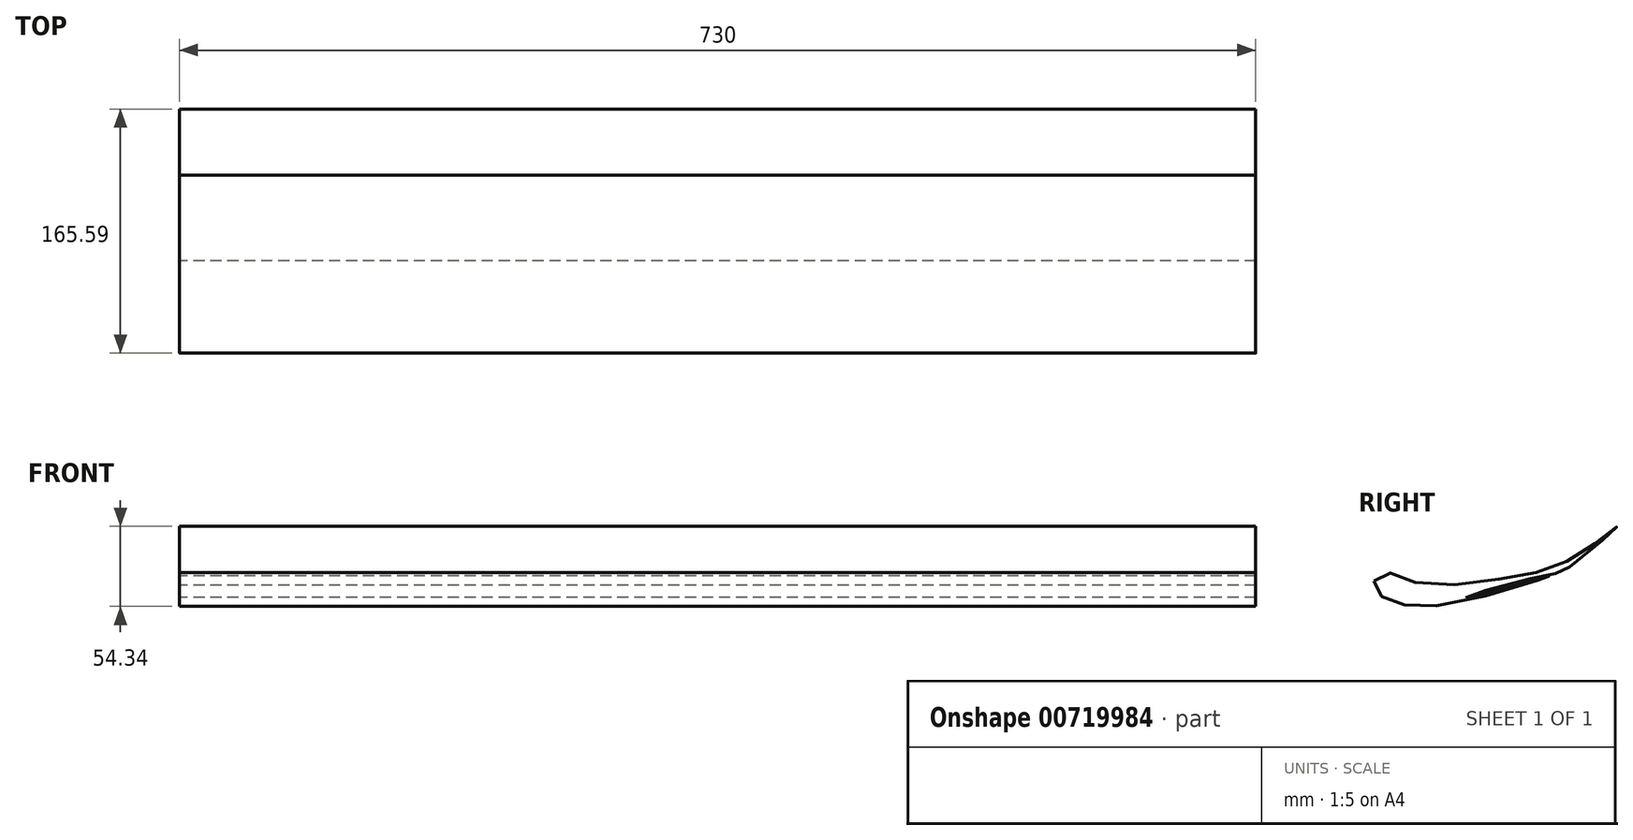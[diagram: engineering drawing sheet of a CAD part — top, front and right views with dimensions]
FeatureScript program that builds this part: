
annotation { "Feature Type Name" : "Feature", "Feature Type Description" : "" }
export const myFeature = defineFeature(function(context is Context, id is Id, definition is map)
    precondition{}
    {
        {
            var Q0;
            Q0=qCreatedBy(makeId("Right.planeOp"),FACE);
            var sketch = newSketch(context, id + "F0", { "sketchPlane" : qUnion([Q0])});
            skFitSpline(sketch, "E0", {"points": [v(-91.57, -32.12) * mm, v(-88.6, -40.7) * mm, v(-73.22, -47.81) * mm, v(-31.77, -46.04) * mm, v(28.63, -28.57) * mm, v(22.4, -30.35) * mm, v(2.28, -35.67) * mm, v(-29.1, -43.08) * mm, v(-25.85, -41.6) * mm, v(24.78, -28.27) * mm, v(33.07, -26.8) * mm, v(42.25, -21.76) * mm, v(73.63, 4.88) * mm, v(63.86, -2.52) * mm, v(34.25, -21.17) * mm, v(-3.64, -30.35) * mm, v(-61.08, -33.6) * mm, v(-82.4, -26.5) * mm, v(-91.57, -32.12) * mm]});
            skSolve(sketch);
        }
        {
            var Q0;
            Q0 = qSketchRegion(id + "F0", true);
            extrude(context, id + "F1", {"entities" : qUnion([Q0]), "endBound" : BoundingType.SYMMETRIC, "depth" : 730 * mm, "offsetDistance" : 25 * mm});
        }
        {
            var Q0;
            Q0=qCreatedBy(makeId("Right.planeOp"),FACE);
            var sketch = newSketch(context, id + "F2", { "sketchPlane" : qUnion([Q0])});
            skFitSpline(sketch, "E1", {"points": [v(48.46, -3.4) * mm, v(49.05, -6.96) * mm, v(55.86, -3.7) * mm, v(68.9, 7.55) * mm, v(82.8, 30.64) * mm, v(100.86, 72.38) * mm, v(89.61, 49) * mm, v(74.52, 20.28) * mm, v(58.82, 6.37) * mm, v(48.76, 0) * mm, v(48.46, -3.4) * mm]});
            skSolve(sketch);
        }
        {
            var Q0;
            Q0=sQuery(id+"F2.wireOp",EDGE,"E1");
            extrude(context, id + "F3", {"bodyType" : ToolBodyType.SURFACE, "surfaceEntities" : qUnion([Q0]), "endBound" : BoundingType.SYMMETRIC, "depth" : 730 * mm, "offsetDistance" : 25 * mm});
        }
    });
